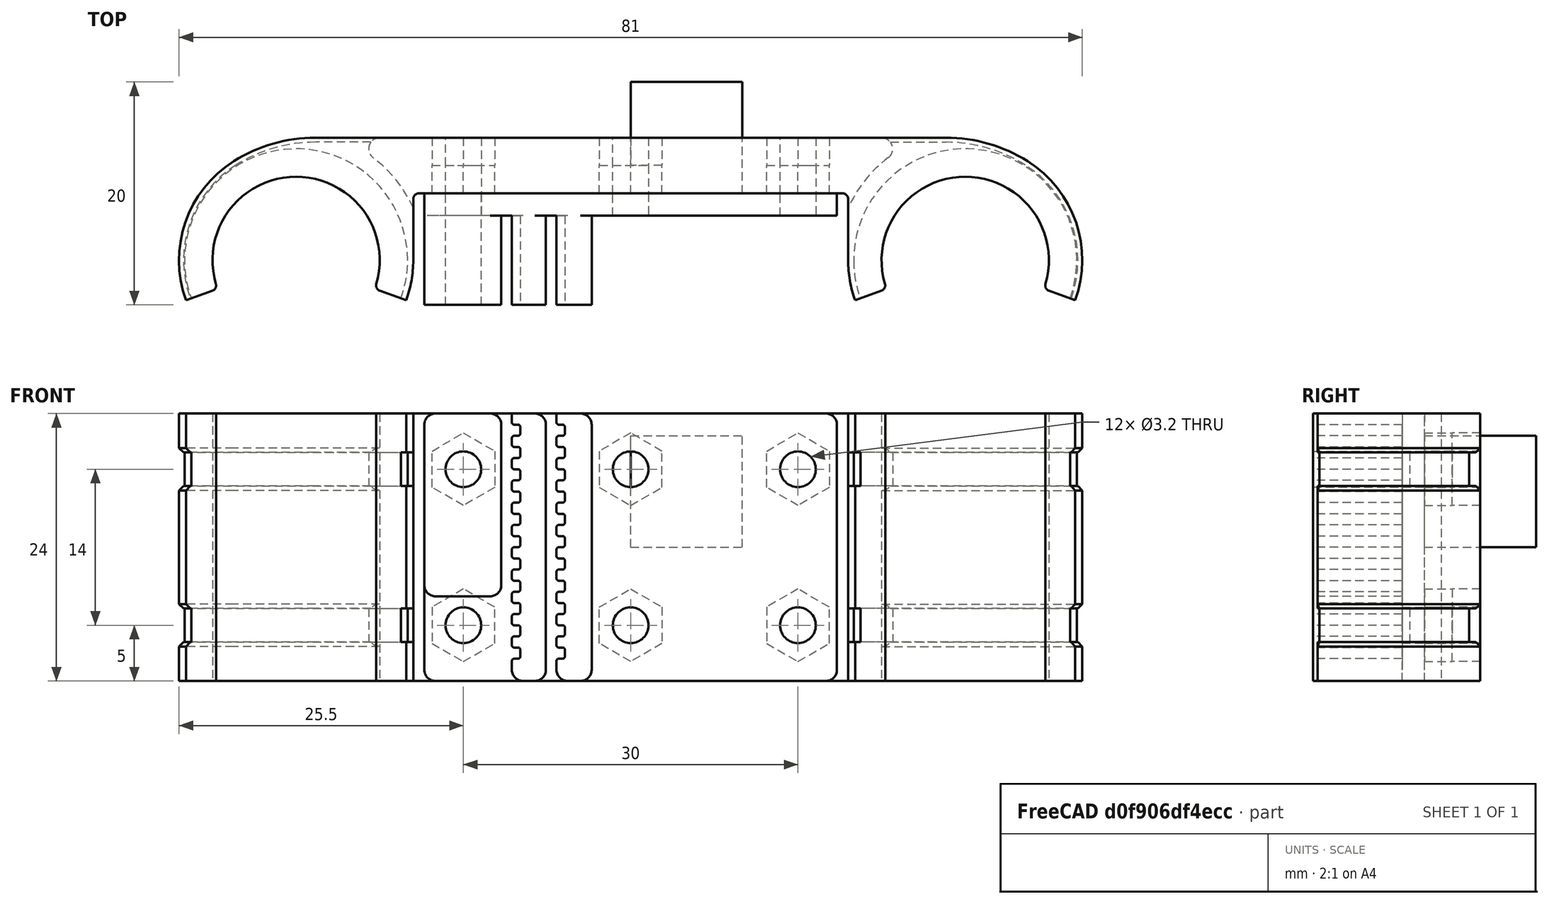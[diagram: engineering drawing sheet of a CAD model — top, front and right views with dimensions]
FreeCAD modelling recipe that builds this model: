
FCSTD DOCUMENT  (FreeCAD 0.16R6712 (Git))
Label: belt_holder_v1
License: All rights reserved
LicenseURL: http://en.wikipedia.org/wiki/All_rights_reserved
objects: Sketcher::SketchObject×4, PartDesign::Pad×4, Mesh::Feature×4, PartDesign::Fillet×3, Part::Feature×2, Part::MultiFuse×2, App::DocumentObjectGroup×1, Part::FeaturePython×1, Part::Box×1, Part::Cut×1
note: 22 computed .brp shape members not serialized (recipe doc carries the construction recipe); baked Part::Feature solids carry a one-line shape summary decoded from their .brp

FEATURE [Part::Feature] Fillet001001  label="Universal_carriage-v1"
  Placement = pos=(0,-6,0) rot=(0,0,1;3.14159rad)
  shape: bbox 81 x 14.59 x 24 mm, 128 faces (baked)
FEATURE [Sketcher::SketchObject] Sketch
  Placement = pos=(0,0,0) rot=(-1,0,0;4.71239rad)
  sketch-geometry (13):
    g0: Circle CenterX=-15 CenterY=-7 CenterZ=0 NormalX=0 NormalY=0 NormalZ=1 Radius=1.6
    g1: Circle CenterX=15 CenterY=-7 CenterZ=0 NormalX=0 NormalY=0 NormalZ=1 Radius=1.6
    g2: Circle CenterX=0 CenterY=7 CenterZ=0 NormalX=0 NormalY=0 NormalZ=1 Radius=1.6
    g3: LineSegment [constr] StartX=15 StartY=-7 StartZ=0 EndX=-15 EndY=-7 EndZ=0
    g4: LineSegment [constr] StartX=-15 StartY=-7 StartZ=0 EndX=-15 EndY=0 EndZ=0
    g5: LineSegment [constr] StartX=0 StartY=7 StartZ=0 EndX=0 EndY=0 EndZ=0
    g6: LineSegment StartX=-18.5 StartY=12 StartZ=0 EndX=18.5 EndY=12 EndZ=0
    g7: LineSegment StartX=18.5 StartY=12 StartZ=0 EndX=18.5 EndY=-12 EndZ=0
    g8: LineSegment StartX=18.5 StartY=-12 StartZ=0 EndX=-18.5 EndY=-12 EndZ=0
    g9: LineSegment StartX=-18.5 StartY=-12 StartZ=0 EndX=-18.5 EndY=12 EndZ=0
    g10: Circle CenterX=-15 CenterY=7 CenterZ=0 NormalX=0 NormalY=0 NormalZ=1 Radius=1.6
    g11: Circle CenterX=15 CenterY=7 CenterZ=0 NormalX=0 NormalY=0 NormalZ=1 Radius=1.6
    g12: Circle CenterX=0 CenterY=-7 CenterZ=0 NormalX=0 NormalY=0 NormalZ=1 Radius=1.6
  constraints (35):
    c: PointOnObject(g2,g-2)
    c: Coincident(g3,g1)
    c: Coincident(g3,g0)
    c: Horizontal(g3)
    c: Coincident(g4,g0)
    c: PointOnObject(g4,g-1)
    c: Vertical(g4)
    c: Coincident(g5,g2)
    c: Coincident(g5,g-1)
    c: Equal(g4,g5)
    c: Equal(g0,g1)
    c: Equal(g1,g2)
    c: DistanceX(g3,g3) = 30
    c: Radius(g0) = 1.6
    c: DistanceY(g5,g5) = 7
    c: Coincident(g6,g7)
    c: Coincident(g7,g8)
    c: Coincident(g8,g9)
    c: Coincident(g9,g6)
    c: Horizontal(g6)
    c: Horizontal(g8)
    c: Vertical(g7)
    c: Vertical(g9)
    c: Symmetric(g6,g8,g-1)
    c: Symmetric(g6,g6,g-2)
    c: DistanceY(g9,g9) = 24
    c: DistanceX(g6,g6) = 37
    c: PointOnObject(g12,g-2)
    c: Equal(g12,g10)
    c: Equal(g10,g11)
    c: Equal(g11,g2)
    c: Symmetric(g12,g2,g-1)
    c: Symmetric(g0,g10,g-1)
    c: Symmetric(g11,g1,g-1)
    c: Symmetric(g0,g1,g-2)
FEATURE [PartDesign::Pad] Pad
  Length = 2
  Length2 = 100
  Placement = pos=(0,0,0) rot=(-1,0,0;4.71239rad)
  Sketch = -> Sketch
  Type = 0
FEATURE [Mesh::Feature] MagCarriage
  Placement = pos=(-40,-2,-12) rot=(0.57735,0.57735,0.57735;2.0944rad)
FEATURE [Mesh::Feature] carriage001  label="carriage"
  Placement = pos=(0,-6,0) rot=(0,0,1;3.14159rad)
FEATURE [Mesh::Feature] idler_end_v3
FEATURE [Mesh::Feature] carriage
  Placement = pos=(0,-6,0) rot=(0,0,1;3.14159rad)
FEATURE [App::DocumentObjectGroup] Group  label="External"
  Group = -> [Fillet001001,carriage,carriage001,MagCarriage,idler_end_v3]
FEATURE [Sketcher::SketchObject] Sketch001
  Placement = pos=(0,-2,0) rot=(-1,0,0;4.71239rad)
  expr: Constraints[6] = 37 / 2
  sketch-geometry (9):
    g0: LineSegment StartX=-18.5 StartY=12 StartZ=0 EndX=-3.5 EndY=12 EndZ=0
    g1: LineSegment StartX=-3.5 StartY=12 StartZ=0 EndX=-3.5 EndY=-12 EndZ=0
    g2: LineSegment StartX=-3.5 StartY=-12 StartZ=0 EndX=-11.5 EndY=-12 EndZ=0
    g3: LineSegment StartX=-18.5 StartY=12 StartZ=0 EndX=-18.5 EndY=-4.4 EndZ=0
    g4: LineSegment StartX=-11.5 StartY=-4.4 StartZ=0 EndX=-18.5 EndY=-4.4 EndZ=0
    g5: LineSegment StartX=-11.5 StartY=-4.4 StartZ=0 EndX=-11.5 EndY=-9.6 EndZ=0
    g6: GeomPoint [constr] X=-11.5 Y=-7 Z=0
    g7: LineSegment StartX=-11.5 StartY=-9.6 StartZ=0 EndX=-11.5 EndY=-12 EndZ=0
    g8: Circle CenterX=-15 CenterY=7 CenterZ=0 NormalX=0 NormalY=0 NormalZ=1 Radius=1.6
  constraints (26):
    c: Coincident(g0,g1)
    c: Coincident(g1,g2)
    c: Horizontal(g0)
    c: Horizontal(g2)
    c: Vertical(g1)
    c: Symmetric(g0,g1,g-1)
    c: DistanceX(g0,g-1) = 18.5
    c: DistanceX(g0,g0) = 15
    c: Coincident(g0,g3)
    c: Vertical(g3)
    c: Coincident(g4,g3)
    c: Horizontal(g4)
    c: Coincident(g4,g5)
    c: Vertical(g5)
    c: PointOnObject(g6,g5)
    c: Symmetric(g4,g5,g6)
    c: DistanceY(g6,g-1) = 7
    c: DistanceX(g4,g4) = 7
    c: DistanceY(g5,g5) = 5.2
    c: Coincident(g7,g5)
    c: Vertical(g7)
    c: Coincident(g2,g7)
    c: DistanceY(g1,g1) = 24
    c: DistanceX(g8,g-1) = 15
    c: DistanceY(g-1,g8) = 7
    c: Radius(g8) = 1.6
FEATURE [PartDesign::Pad] Pad001
  Length = 8
  Length2 = 100
  Placement = pos=(0,-2,0) rot=(-1,0,0;4.71239rad)
  Sketch = -> Sketch001
  Type = 0
FEATURE [Sketcher::SketchObject] Sketch002
  Placement = pos=(0,-2,0) rot=(-1,0,0;4.71239rad)
  sketch-geometry (8):
    g0: LineSegment StartX=-6.65 StartY=12 StartZ=0 EndX=-6.65 EndY=11 EndZ=0
    g1: LineSegment StartX=-6.65 StartY=11 StartZ=0 EndX=-5.9 EndY=11 EndZ=0
    g2: LineSegment StartX=-5.9 StartY=11 StartZ=0 EndX=-5.9 EndY=10 EndZ=0
    g3: LineSegment StartX=-5.9 StartY=10 StartZ=0 EndX=-6.65 EndY=10 EndZ=0
    g4: LineSegment StartX=-7.6 StartY=9 StartZ=0 EndX=-7.6 EndY=12 EndZ=0
    g5: LineSegment StartX=-7.6 StartY=12 StartZ=0 EndX=-6.65 EndY=12 EndZ=0
    g6: LineSegment StartX=-6.65 StartY=10 StartZ=0 EndX=-6.65 EndY=9 EndZ=0
    g7: LineSegment StartX=-6.65 StartY=9 StartZ=0 EndX=-7.6 EndY=9 EndZ=0
  constraints (24):
    c: Vertical(g0)
    c: Coincident(g0,g1)
    c: Horizontal(g1)
    c: Coincident(g1,g2)
    c: Vertical(g2)
    c: Coincident(g2,g3)
    c: Horizontal(g3)
    c: Vertical(g4)
    c: Coincident(g4,g5)
    c: Coincident(g5,g0)
    c: Horizontal(g5)
    c: DistanceX(g5,g5) = 0.95
    c: DistanceX(g1,g1) = 0.75
    c: DistanceY(g0,g0) = 1
    c: Equal(g2,g0)
    c: DistanceY(g-1,g4) = 12
    c: DistanceX(g4,g-1) = 7.6
    c: Coincident(g3,g6)
    c: Vertical(g6)
    c: Coincident(g6,g7)
    c: Horizontal(g7)
    c: Coincident(g4,g7)
    c: Equal(g6,g2)
    c: Equal(g3,g1)
FEATURE [PartDesign::Pad] Pad002
  Length = 10
  Length2 = 100
  Placement = pos=(0,-2,0) rot=(-1,0,0;4.71239rad)
  Sketch = -> Sketch002
  Type = 0
FEATURE [PartDesign::Fillet] Fillet
  Base = -> Pad002 [Edge2,Edge5,Edge8,Edge11]
  Placement = pos=(0,-2,0) rot=(-1,0,0;4.71239rad)
  Radius = 0.2
FEATURE [Part::FeaturePython] Array  # Draft array (typed FeaturePython)
  Angle = 360
  ArrayType = 0
  Axis = (0,0,1)
  Base = -> Fillet
  Center = (0,0,0)
  Fuse = true
  IntervalAxis = (0,0,0)
  IntervalX = (-4,0,0)
  IntervalY = (0,1,0)
  IntervalZ = (0,0,-2)
  NumberPolar = 1
  NumberX = 2
  NumberY = 1
  NumberZ = 11
FEATURE [Part::Box] Box  label="Cube"
  Height = 10
  Length = 10
  Width = 10
FEATURE [Sketcher::SketchObject] Sketch003
  Placement = pos=(0,-2,0) rot=(-1,0,0;4.71239rad)
  sketch-geometry (9):
    g0: LineSegment StartX=-10.65 StartY=-10.8418 StartZ=0 EndX=-10.65 EndY=-12 EndZ=0
    g1: LineSegment StartX=-10.65 StartY=-12 StartZ=0 EndX=-7.6 EndY=-12 EndZ=0
    g2: LineSegment StartX=-7.6 StartY=-12 StartZ=0 EndX=-7.6 EndY=-10.8418 EndZ=0
    g3: LineSegment StartX=-7.6 StartY=-10.8418 StartZ=0 EndX=-6.65 EndY=-10.8418 EndZ=0
    g4: LineSegment StartX=-6.65 StartY=-10.8418 StartZ=0 EndX=-6.65 EndY=-12.6409 EndZ=0
    g5: LineSegment StartX=-6.65 StartY=-12.6409 StartZ=0 EndX=-11.6 EndY=-12.6409 EndZ=0
    g6: LineSegment StartX=-11.6 StartY=-12.6409 StartZ=0 EndX=-11.6 EndY=-10.8418 EndZ=0
    g7: LineSegment StartX=-11.6 StartY=-10.8418 StartZ=0 EndX=-10.65 EndY=-10.8418 EndZ=0
    g8: LineSegment [constr] StartX=-10.65 StartY=-10.8418 StartZ=0 EndX=-7.6 EndY=-10.8418 EndZ=0
  constraints (24):
    c: Vertical(g0)
    c: Coincident(g0,g1)
    c: Horizontal(g1)
    c: Coincident(g1,g2)
    c: Vertical(g2)
    c: Coincident(g2,g3)
    c: Horizontal(g3)
    c: Coincident(g3,g4)
    c: Vertical(g4)
    c: Coincident(g4,g5)
    c: Horizontal(g5)
    c: Coincident(g5,g6)
    c: Vertical(g6)
    c: Coincident(g6,g7)
    c: Coincident(g7,g0)
    c: Horizontal(g7)
    c: Equal(g7,g3)
    c: DistanceX(g7,g7) = 0.95
    c: DistanceX(g6,g2) = 4
    c: DistanceX(g6,g-1) = 11.6
    c: DistanceY(g0,g-1) = 12
    c: Coincident(g8,g0)
    c: Coincident(g8,g2)
    c: Horizontal(g8)
FEATURE [PartDesign::Pad] Pad003
  Length = 10
  Length2 = 100
  Placement = pos=(0,-2,0) rot=(-1,0,0;4.71239rad)
  Sketch = -> Sketch003
  Type = 0
FEATURE [Part::MultiFuse] Fusion
  Shapes = -> [Pad003,Array]
FEATURE [Part::Cut] Cut
  Base = -> Pad001
  Tool = -> Fusion
FEATURE [Part::MultiFuse] Fusion001
  Shapes = -> [Pad,Cut]
FEATURE [Part::Feature] Fusion001001  label="Fusion001"
  shape: bbox 37 x 10 x 24 mm, 199 faces (baked)
FEATURE [PartDesign::Fillet] Fillet001002
  Base = -> Fusion001001 [Edge589,Edge587,Edge308,Edge306,Edge586,Edge122,Edge585,Edge305,Edge590,Edge121,Edge12,Edge11]
  Radius = 1
FEATURE [PartDesign::Fillet] Fillet001003
  Base = -> Fillet001002 [Edge57]
  Radius = 1
